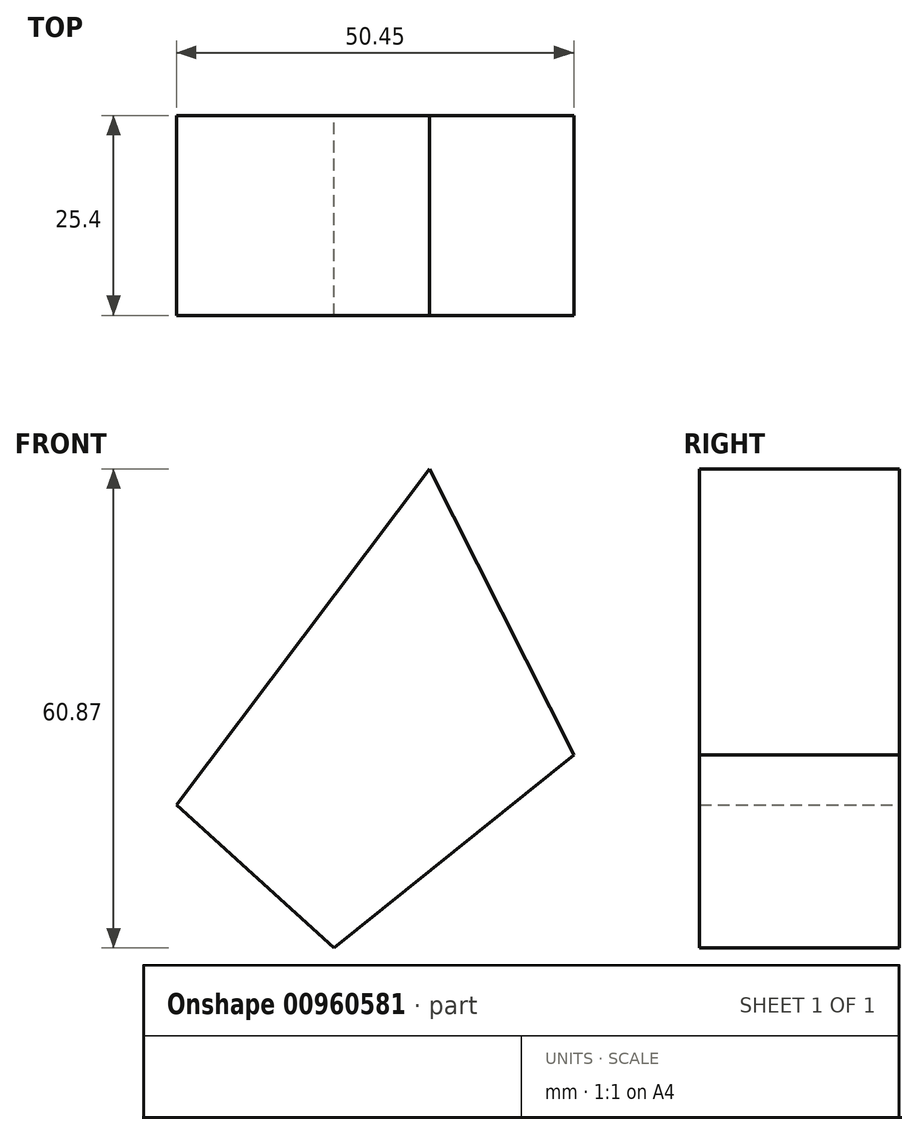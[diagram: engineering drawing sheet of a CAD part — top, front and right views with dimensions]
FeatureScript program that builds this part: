
annotation { "Feature Type Name" : "Feature", "Feature Type Description" : "" }
export const myFeature = defineFeature(function(context is Context, id is Id, definition is map)
    precondition{}
    {
        {
            var Q0;
            Q0=qCreatedBy(makeId("Front.planeOp"),FACE);
            var sketch = newSketch(context, id + "F0", { "sketchPlane" : qUnion([Q0])});
            skLineSegment(sketch, "E0", {"start": v(0, 0) * mm, "end": v(30.43, 24.52) * mm});
            skLineSegment(sketch, "E1", {"start": v(30.43, 24.52) * mm, "end": v(12.09, 60.87) * mm});
            skLineSegment(sketch, "E2", {"start": v(12.09, 60.87) * mm, "end": v(-20.02, 18.17) * mm});
            skLineSegment(sketch, "E3", {"start": v(-20.02, 18.17) * mm, "end": v(0, 0) * mm});
            skSolve(sketch);
        }
        {
            var Q0;
            Q0 = qSketchRegion(id + "F0", true);
            extrude(context, id + "F1", {"entities" : qUnion([Q0]), "depth" : 25.4 * mm, "offsetDistance" : 25.4 * mm});
        }
    });
